# Revit family: Sanitary-Hand-&-Hair-Dryers-Sloan-Valve-EHD-501_
name_source: partatom
category: Specialty Equipment
units: mm (PartAtom-declared; Revit-internal decimal feet)

## family parameters
Cut with Voids When Loaded = No
Host = Face
OmniClass Number = 23.40.20.21.14
OmniClass Title = Hand and Hair Dryers
Part Type = Normal
Room Calculation Point = No
Round Connector Dimension = Use Diameter
Shared = No

## types (10) — shared parameters
Apparent Load = 1356 VA
Assembly Code = C1030200
Connector Description = Electrical Connection
Current = 11 A
Default Elevation = 0"
Depth = 6 7/8"
Edition number = 1
Height = 12 7/8"
Keynote = 15410
Manufacturer = Sloan Valve
Number of Poles = 1
Power Factor = 1
Product data url = https://bimobject.com
URL = www.sloanvalve.com
Voltage = 120 V
Width = 11 15/16"

## per-type parameters (varying)
| type | Description | Part Number | Product Material |
| EHD-501-BN | Sloan® XLERATOR® Sensor-Operated Wall - Surface Hand Dryer EHD-501 110/120V, Sloan® XLERATOR® Sensor-Operated Wall - Surface Hand Dryer. | 3366122 | Sloan Valve - Finish - Brushed Nickel |
| EHD-501-BN-HEPA | Sloan® XLERATOR® Sensor-Operated Wall - Surface Hand Dryer EHD-501, HEPA110/120V, Sloan® XLERATOR® Sensor-Operated Wall - Surface Hand Dryer. | 3366123 | Sloan Valve - Finish - Brushed Nickel |
| EHD-501-CP | Sloan® XLERATOR® Sensor-Operated Wall - Surface Hand Dryer EHD-501 110/120V, Sloan® XLERATOR® Sensor-Operated Wall - Surface Hand Dryer. | 3366051 | Sloan Valve - Finish - Polished Chrome |
| EHD-501-CP-HEPA | Sloan® XLERATOR® Sensor-Operated Wall - Surface Hand Dryer EHD-501, HEPA110/120V, Sloan® XLERATOR® Sensor-Operated Wall - Surface Hand Dryer. | 3366120 | Sloan Valve - Finish - Polished Chrome |
| EHD-501-GR | Sloan® XLERATOR® Sensor-Operated Wall - Surface Hand Dryer EHD-501 110/120V, Sloan® XLERATOR® Sensor-Operated Wall - Surface Hand Dryer. | 3366061 | Sloan Valve - Finish - Graphite |
| EHD-501-GR-HEPA | Sloan® XLERATOR® Sensor-Operated Wall - Surface Hand Dryer EHD-501, HEPA110/120V, Sloan® XLERATOR® Sensor-Operated Wall - Surface Hand Dryer. | 3366121 | Sloan Valve - Finish - Graphite |
| EHD-501-MW | Sloan® XLERATOR® Sensor-Operated Wall - Surface Hand Dryer EHD-501 110/120V, Sloan® XLERATOR® Sensor-Operated Wall - Surface Hand Dryer. | 3366070 | Sloan Valve - Finish - Matte White |
| EHD-501-MW-HEPA | Sloan® XLERATOR® Sensor-Operated Wall - Surface Hand Dryer EHD-501, HEPA110/120V, Sloan® XLERATOR® Sensor-Operated Wall - Surface Hand Dryer. | 3366119 | Sloan Valve - Finish - Matte White |
| EHD-501-PW | Sloan® XLERATOR® Sensor-Operated Wall - Surface Hand Dryer EHD-501 110/120V, Sloan® XLERATOR® Sensor-Operated Wall - Surface Hand Dryer. | 3366050 | Sloan Valve - Finish - Polished White |
| EHD-501-PW-HEPA | Sloan® XLERATOR® Sensor-Operated Wall - Surface Hand Dryer EHD-501, HEPA110/120V, Sloan® XLERATOR® Sensor-Operated Wall - Surface Hand Dryer. | 3366142 | Sloan Valve - Finish - Polished White |

note: column(s) folded — value = type name in every type: Model

## geometry (parser evidence)
native form markers: Sweep x3
no freeform markers — native parametric forms only
